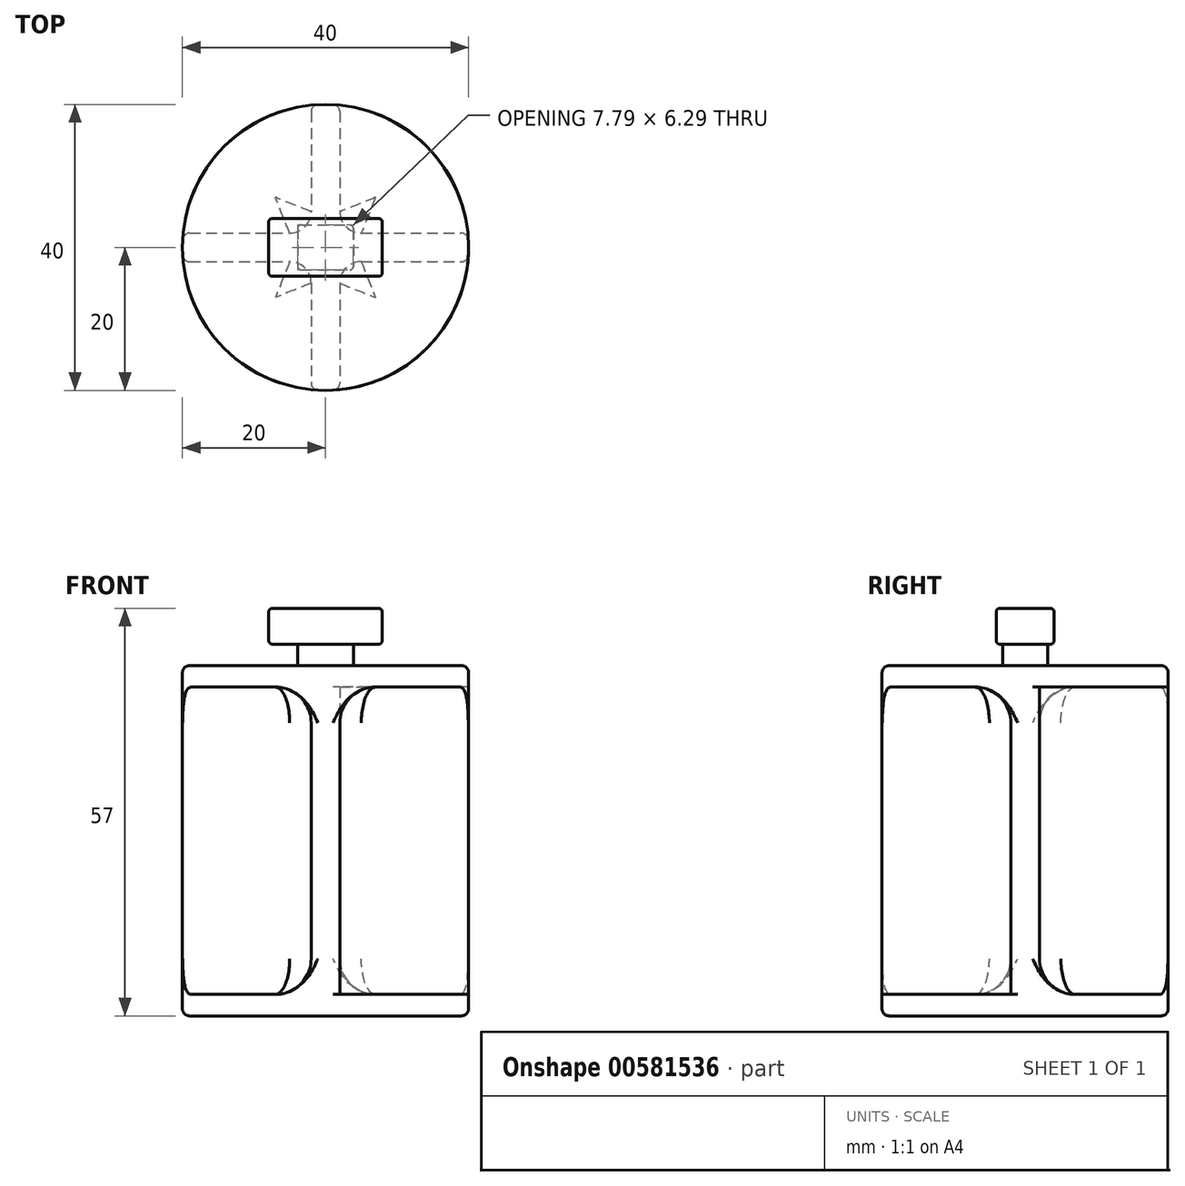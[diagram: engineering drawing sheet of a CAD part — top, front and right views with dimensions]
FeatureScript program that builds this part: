
annotation { "Feature Type Name" : "Feature", "Feature Type Description" : "" }
export const myFeature = defineFeature(function(context is Context, id is Id, definition is map)
    precondition{}
    {
        {
            var Q0;
            Q0=qCreatedBy(makeId("Top.planeOp"),FACE);
            var sketch = newSketch(context, id + "F0", { "sketchPlane" : qUnion([Q0])});
            skCircle(sketch, "E0", {"center": v(0, 0) * mm, "radius": 20 * mm});
            skLineSegment(sketch, "E1", {"start": v(0, -2) * mm, "end": v(0, -20) * mm});
            skLineSegment(sketch, "E2.0", {"start": v(-2, 20) * mm, "end": v(-2, 5) * mm});
            skLineSegment(sketch, "E3.0", {"start": v(2, 20) * mm, "end": v(2, 5) * mm});
            skLineSegment(sketch, "E4.0", {"start": v(-20, -2) * mm, "end": v(-5, -2) * mm});
            skLineSegment(sketch, "E5.0", {"start": v(-20, 2) * mm, "end": v(-5, 2) * mm});
            skPoint(sketch, "E6.orphan", {"position": v(0, 20) * mm});
            skLineSegment(sketch, "E7.trimOffspring", {"start": v(2, -5) * mm, "end": v(2, -20) * mm});
            skLineSegment(sketch, "E8.trimOffspring", {"start": v(-2, -5) * mm, "end": v(-2, -20) * mm});
            skPoint(sketch, "E9.start.orphan", {"position": v(-20, 0) * mm});
            skArc(sketch, "E10.filletArc", {"start": v(-2, -5) * mm, "mid": v(-2.88, -2.88) * mm, "end": v(-5, -2) * mm});
            skLineSegment(sketch, "E11", {"start": v(5, -2) * mm, "end": v(19.9, -2) * mm});
            skPoint(sketch, "E12.visualSharp", {"position": v(2, -2) * mm});
            skArc(sketch, "E12.filletArc", {"start": v(5, -2) * mm, "mid": v(2.88, -2.88) * mm, "end": v(2, -5) * mm});
            skArc(sketch, "E13.filletArc", {"start": v(-5, 2) * mm, "mid": v(-2.88, 2.88) * mm, "end": v(-2, 5) * mm});
            skLineSegment(sketch, "E14", {"start": v(5, 2) * mm, "end": v(19.9, 2) * mm});
            skPoint(sketch, "E15.visualSharp", {"position": v(2, 2) * mm});
            skArc(sketch, "E15.filletArc", {"start": v(2, 5) * mm, "mid": v(2.88, 2.88) * mm, "end": v(5, 2) * mm});
            skSolve(sketch);
        }
        {
            var Q0;
            {var subQ4=sQuery(id+"F0.wireOp",EDGE,"E10.filletArc");Q0=makeQuery(id+"F0.imprint","IMPRINT",FACE,{"disambiguationData":[TD([[makeQuery(id+"F0.imprint","IMPRINT",EDGE,{"derivedFrom":subQ4}),-1.0]])]});}
            extrude(context, id + "F1", {"entities" : qUnion([Q0]), "depth" : 43 * mm, "offsetDistance" : 25 * mm});
        }
        {
            var Q0;
            Q0=makeQuery(id+"F1.opExtrude","CAP_FACE",FACE,{"disambiguationData":[OSD([sQuery(id+"F0.wireOp",EDGE,"E0"),sQuery(id+"F0.wireOp",EDGE,"E2.0"),sQuery(id+"F0.wireOp",EDGE,"E3.0"),sQuery(id+"F0.wireOp",EDGE,"E4.0"),sQuery(id+"F0.wireOp",EDGE,"E5.0"),sQuery(id+"F0.wireOp",EDGE,"E7.trimOffspring"),sQuery(id+"F0.wireOp",EDGE,"E8.trimOffspring"),sQuery(id+"F0.wireOp",EDGE,"E10.filletArc"),sQuery(id+"F0.wireOp",EDGE,"E11"),sQuery(id+"F0.wireOp",EDGE,"E12.filletArc"),sQuery(id+"F0.wireOp",EDGE,"E13.filletArc"),sQuery(id+"F0.wireOp",EDGE,"E14"),sQuery(id+"F0.wireOp",EDGE,"E15.filletArc")])],"isStart":true});
            var sketch = newSketch(context, id + "F2", { "sketchPlane" : qUnion([Q0])});
            skCircle(sketch, "E16", {"center": v(0, 0) * mm, "radius": 20 * mm});
            skSolve(sketch);
        }
        {
            var Q0;
            {var subQ2=makeQuery(id+"F1.opExtrude","CAP_EDGE",EDGE,{"disambiguationData":[OSD([sQuery(id+"F0.wireOp",EDGE,"E7.trimOffspring")])],"isStart":true});Q0=makeQuery(id+"F2.imprint","IMPRINT",FACE,{"disambiguationData":[TD([[makeQuery(id+"F2.imprint","IMPRINT",EDGE,{"derivedFrom":subQ2}),-1.0]])]});}
            var Q1;
            {var subQ4=makeQuery(id+"F1.opExtrude","CAP_EDGE",EDGE,{"disambiguationData":[OSD([sQuery(id+"F0.wireOp",EDGE,"E2.0")])],"isStart":true});Q1=makeQuery(id+"F2.imprint","IMPRINT",FACE,{"disambiguationData":[TD([[makeQuery(id+"F2.imprint","IMPRINT",EDGE,{"derivedFrom":subQ4}),-1.0]])]});}
            var Q2;
            {var subQ1=makeQuery(id+"F1.opExtrude","CAP_EDGE",EDGE,{"disambiguationData":[OSD([sQuery(id+"F0.wireOp",EDGE,"E4.0")])],"isStart":true});Q2=makeQuery(id+"F2.imprint","IMPRINT",FACE,{"disambiguationData":[TD([[makeQuery(id+"F2.imprint","IMPRINT",EDGE,{"derivedFrom":subQ1}),1.0]])]});}
            var Q3;
            {var subQ1=makeQuery(id+"F1.opExtrude","CAP_EDGE",EDGE,{"disambiguationData":[OSD([sQuery(id+"F0.wireOp",EDGE,"E2.0")])],"isStart":true});Q3=makeQuery(id+"F2.imprint","IMPRINT",FACE,{"disambiguationData":[TD([[makeQuery(id+"F2.imprint","IMPRINT",EDGE,{"derivedFrom":subQ1}),1.0]])]});}
            var Q4;
            {var subQ2=makeQuery(id+"F1.opExtrude","CAP_EDGE",EDGE,{"disambiguationData":[OSD([sQuery(id+"F0.wireOp",EDGE,"E3.0")])],"isStart":true});Q4=makeQuery(id+"F2.imprint","IMPRINT",FACE,{"disambiguationData":[TD([[makeQuery(id+"F2.imprint","IMPRINT",EDGE,{"derivedFrom":subQ2}),-1.0]])]});}
            extrude(context, id + "F3", {"entities" : qUnion([Q0, Q1, Q2, Q3, Q4]), "operationType" : NewBodyOperationType.ADD, "depth" : 3 * mm, "offsetDistance" : 25 * mm});
        }
        {
            var Q0;
            Q0=makeQuery(id+"F1.opExtrude","CAP_FACE",FACE,{"disambiguationData":[OSD([sQuery(id+"F0.wireOp",EDGE,"E0"),sQuery(id+"F0.wireOp",EDGE,"E2.0"),sQuery(id+"F0.wireOp",EDGE,"E3.0"),sQuery(id+"F0.wireOp",EDGE,"E4.0"),sQuery(id+"F0.wireOp",EDGE,"E5.0"),sQuery(id+"F0.wireOp",EDGE,"E7.trimOffspring"),sQuery(id+"F0.wireOp",EDGE,"E8.trimOffspring"),sQuery(id+"F0.wireOp",EDGE,"E10.filletArc"),sQuery(id+"F0.wireOp",EDGE,"E11"),sQuery(id+"F0.wireOp",EDGE,"E12.filletArc"),sQuery(id+"F0.wireOp",EDGE,"E13.filletArc"),sQuery(id+"F0.wireOp",EDGE,"E14"),sQuery(id+"F0.wireOp",EDGE,"E15.filletArc")])],"isStart":false});
            var sketch = newSketch(context, id + "F4", { "sketchPlane" : qUnion([Q0])});
            skCircle(sketch, "E17", {"center": v(0, 0) * mm, "radius": 20 * mm});
            skSolve(sketch);
        }
        {
            var Q0;
            {var subQ1=makeQuery(id+"F1.opExtrude","CAP_EDGE",EDGE,{"disambiguationData":[OSD([sQuery(id+"F0.wireOp",EDGE,"E2.0")])],"isStart":false});Q0=makeQuery(id+"F4.imprint","IMPRINT",FACE,{"disambiguationData":[TD([[makeQuery(id+"F4.imprint","IMPRINT",EDGE,{"derivedFrom":subQ1}),-1.0]])]});}
            var Q1;
            {var subQ2=makeQuery(id+"F1.opExtrude","CAP_EDGE",EDGE,{"disambiguationData":[OSD([sQuery(id+"F0.wireOp",EDGE,"E3.0")])],"isStart":false});Q1=makeQuery(id+"F4.imprint","IMPRINT",FACE,{"disambiguationData":[TD([[makeQuery(id+"F4.imprint","IMPRINT",EDGE,{"derivedFrom":subQ2}),1.0]])]});}
            var Q2;
            {var subQ2=makeQuery(id+"F1.opExtrude","CAP_EDGE",EDGE,{"disambiguationData":[OSD([sQuery(id+"F0.wireOp",EDGE,"E7.trimOffspring")])],"isStart":false});Q2=makeQuery(id+"F4.imprint","IMPRINT",FACE,{"disambiguationData":[TD([[makeQuery(id+"F4.imprint","IMPRINT",EDGE,{"derivedFrom":subQ2}),1.0]])]});}
            var Q3;
            {var subQ1=makeQuery(id+"F1.opExtrude","CAP_EDGE",EDGE,{"disambiguationData":[OSD([sQuery(id+"F0.wireOp",EDGE,"E4.0")])],"isStart":false});Q3=makeQuery(id+"F4.imprint","IMPRINT",FACE,{"disambiguationData":[TD([[makeQuery(id+"F4.imprint","IMPRINT",EDGE,{"derivedFrom":subQ1}),-1.0]])]});}
            var Q4;
            {var subQ4=makeQuery(id+"F1.opExtrude","CAP_EDGE",EDGE,{"disambiguationData":[OSD([sQuery(id+"F0.wireOp",EDGE,"E2.0")])],"isStart":false});Q4=makeQuery(id+"F4.imprint","IMPRINT",FACE,{"disambiguationData":[TD([[makeQuery(id+"F4.imprint","IMPRINT",EDGE,{"derivedFrom":subQ4}),1.0]])]});}
            extrude(context, id + "F5", {"entities" : qUnion([Q0, Q1, Q2, Q3, Q4]), "operationType" : NewBodyOperationType.ADD, "depth" : 3 * mm, "offsetDistance" : 25 * mm});
        }
        {
            var Q0;
            Q0=makeQuery(id+"F3.opExtrude","CAP_EDGE",EDGE,{"disambiguationData":[OSD([sQuery(id+"F2.wireOp",EDGE,"E16")])],"isStart":false});
            fillet(context, id + "F6", {"entities" : qUnion([Q0]), "radius" : 1 * mm, "tangentPropagation" : true, "allowEdgeOverflow" : false});
        }
        {
            var Q0;
            Q0=makeQuery(id+"F5.opExtrude","CAP_EDGE",EDGE,{"disambiguationData":[OSD([sQuery(id+"F4.wireOp",EDGE,"E17")])],"isStart":false});
            var Q1;
            Q1=makeQuery(id+"F1.opExtrude","SWEPT_EDGE",EDGE,{"disambiguationData":[OSD([sQuery(id+"F0.wireOp",EDGE,"E0"),sQuery(id+"F0.wireOp",EDGE,"E5.0")])]});
            var Q2;
            Q2=makeQuery(id+"F1.opExtrude","SWEPT_EDGE",EDGE,{"disambiguationData":[OSD([sQuery(id+"F0.wireOp",EDGE,"E0"),sQuery(id+"F0.wireOp",EDGE,"E4.0")])]});
            var Q3;
            Q3=makeQuery(id+"F1.opExtrude","SWEPT_EDGE",EDGE,{"disambiguationData":[OSD([sQuery(id+"F0.wireOp",EDGE,"E0"),sQuery(id+"F0.wireOp",EDGE,"E2.0")])]});
            var Q4;
            Q4=makeQuery(id+"F1.opExtrude","SWEPT_EDGE",EDGE,{"disambiguationData":[OSD([sQuery(id+"F0.wireOp",EDGE,"E0"),sQuery(id+"F0.wireOp",EDGE,"E3.0")])]});
            var Q5;
            Q5=makeQuery(id+"F1.opExtrude","SWEPT_EDGE",EDGE,{"disambiguationData":[OSD([sQuery(id+"F0.wireOp",EDGE,"E0"),sQuery(id+"F0.wireOp",EDGE,"E14")])]});
            var Q6;
            Q6=makeQuery(id+"F1.opExtrude","SWEPT_EDGE",EDGE,{"disambiguationData":[OSD([sQuery(id+"F0.wireOp",EDGE,"E0"),sQuery(id+"F0.wireOp",EDGE,"E11")])]});
            var Q7;
            Q7=makeQuery(id+"F1.opExtrude","SWEPT_EDGE",EDGE,{"disambiguationData":[OSD([sQuery(id+"F0.wireOp",EDGE,"E0"),sQuery(id+"F0.wireOp",EDGE,"E7.trimOffspring")])]});
            var Q8;
            Q8=makeQuery(id+"F1.opExtrude","SWEPT_EDGE",EDGE,{"disambiguationData":[OSD([sQuery(id+"F0.wireOp",EDGE,"E0"),sQuery(id+"F0.wireOp",EDGE,"E8.trimOffspring")])]});
            fillet(context, id + "F7", {"entities" : qUnion([Q0, Q1, Q2, Q3, Q4, Q5, Q6, Q7, Q8]), "radius" : 1 * mm, "tangentPropagation" : true, "allowEdgeOverflow" : false});
        }
        {
            var Q0;
            Q0=makeQuery(id+"F5.opExtrude","CAP_FACE",FACE,{"disambiguationData":[OSD([sQuery(id+"F4.wireOp",EDGE,"E17")])],"isStart":false});
            var sketch = newSketch(context, id + "F8", { "sketchPlane" : qUnion([Q0])});
            skLineSegment(sketch, "E18.bottom", {"start": v(-3.9, 3.14) * mm, "end": v(3.9, 3.14) * mm});
            skLineSegment(sketch, "E18.top", {"start": v(-3.9, -3.14) * mm, "end": v(3.9, -3.14) * mm});
            skLineSegment(sketch, "E18.left", {"start": v(-3.9, 3.14) * mm, "end": v(-3.9, -3.14) * mm});
            skLineSegment(sketch, "E18.right", {"start": v(3.9, 3.14) * mm, "end": v(3.9, -3.14) * mm});
            skSolve(sketch);
        }
        {
            var Q0;
            Q0 = qSketchRegion(id + "F8", true);
            extrude(context, id + "F9", {"entities" : qUnion([Q0]), "operationType" : NewBodyOperationType.ADD, "depth" : 3 * mm, "offsetDistance" : 25 * mm});
        }
        {
            var Q0;
            Q0=makeQuery(id+"F9.opExtrude","CAP_FACE",FACE,{"disambiguationData":[OSD([sQuery(id+"F8.wireOp",EDGE,"E18.bottom"),sQuery(id+"F8.wireOp",EDGE,"E18.top"),sQuery(id+"F8.wireOp",EDGE,"E18.left"),sQuery(id+"F8.wireOp",EDGE,"E18.right")])],"isStart":false});
            var sketch = newSketch(context, id + "F10", { "sketchPlane" : qUnion([Q0])});
            skLineSegment(sketch, "E19.bottom", {"start": v(-7.93, 4.05) * mm, "end": v(7.93, 4.05) * mm});
            skLineSegment(sketch, "E19.top", {"start": v(-7.93, -4.05) * mm, "end": v(7.93, -4.05) * mm});
            skLineSegment(sketch, "E19.left", {"start": v(-7.93, 4.05) * mm, "end": v(-7.93, -4.05) * mm});
            skLineSegment(sketch, "E19.right", {"start": v(7.93, 4.05) * mm, "end": v(7.93, -4.05) * mm});
            skPoint(sketch, "E20", {"position": v(0, 4.05) * mm});
            skPoint(sketch, "E21", {"position": v(7.93, 0) * mm});
            skSolve(sketch);
        }
        {
            var Q0;
            Q0=makeQuery(id+"F9.opExtrude","SWEPT_EDGE",EDGE,{"disambiguationData":[OSD([sQuery(id+"F8.wireOp",EDGE,"E18.top"),sQuery(id+"F8.wireOp",EDGE,"E18.right")])]});
            fillet(context, id + "F11", {"entities" : qUnion([Q0]), "radius" : 0.5 * mm, "tangentPropagation" : true, "allowEdgeOverflow" : false});
        }
        {
            var Q0;
            Q0=makeQuery(id+"F9.opExtrude","SWEPT_EDGE",EDGE,{"disambiguationData":[OSD([sQuery(id+"F8.wireOp",EDGE,"E18.top"),sQuery(id+"F8.wireOp",EDGE,"E18.left")])]});
            var Q1;
            Q1=makeQuery(id+"F9.opExtrude","SWEPT_EDGE",EDGE,{"disambiguationData":[OSD([sQuery(id+"F8.wireOp",EDGE,"E18.bottom"),sQuery(id+"F8.wireOp",EDGE,"E18.right")])]});
            var Q2;
            Q2=makeQuery(id+"F9.opExtrude","SWEPT_EDGE",EDGE,{"disambiguationData":[OSD([sQuery(id+"F8.wireOp",EDGE,"E18.bottom"),sQuery(id+"F8.wireOp",EDGE,"E18.left")])]});
            fillet(context, id + "F12", {"entities" : qUnion([Q0, Q1, Q2]), "radius" : .5 * mm, "tangentPropagation" : true, "allowEdgeOverflow" : false});
        }
        {
            var Q0;
            Q0=makeQuery(id+"F10.imprint","IMPRINT",FACE,{"disambiguationData":[TD([[makeQuery(id+"F10.imprint","IMPRINT",EDGE,{"derivedFrom":makeQuery(id+"F9.opExtrude","CAP_EDGE",EDGE,{"disambiguationData":[OSD([sQuery(id+"F8.wireOp",EDGE,"E18.bottom")])],"isStart":false})}),-1.0]])]});
            var Q1;
            Q1=makeQuery(id+"F10.imprint","IMPRINT",FACE,{"disambiguationData":[TD([[makeQuery(id+"F10.imprint","IMPRINT",EDGE,{"derivedFrom":sQuery(id+"F10.wireOp",EDGE,"E19.bottom")}),-1.0]])]});
            extrude(context, id + "F13", {"entities" : qUnion([Q0, Q1]), "operationType" : NewBodyOperationType.ADD, "depth" : 5 * mm, "offsetDistance" : 25 * mm});
        }
        {
            var Q0;
            Q0=makeQuery(id+"F13.opExtrude","SWEPT_EDGE",EDGE,{"disambiguationData":[OSD([sQuery(id+"F10.wireOp",EDGE,"E19.top"),sQuery(id+"F10.wireOp",EDGE,"E19.left")])]});
            var Q1;
            Q1=makeQuery(id+"F13.opExtrude","CAP_EDGE",EDGE,{"disambiguationData":[OSD([sQuery(id+"F10.wireOp",EDGE,"E19.top")])],"isStart":false});
            var Q2;
            Q2=makeQuery(id+"F13.opExtrude","SWEPT_EDGE",EDGE,{"disambiguationData":[OSD([sQuery(id+"F10.wireOp",EDGE,"E19.top"),sQuery(id+"F10.wireOp",EDGE,"E19.right")])]});
            var Q3;
            Q3=makeQuery(id+"F13.opExtrude","SWEPT_EDGE",EDGE,{"disambiguationData":[OSD([sQuery(id+"F10.wireOp",EDGE,"E19.bottom"),sQuery(id+"F10.wireOp",EDGE,"E19.right")])]});
            var Q4;
            Q4=makeQuery(id+"F13.opExtrude","CAP_EDGE",EDGE,{"disambiguationData":[OSD([sQuery(id+"F10.wireOp",EDGE,"E19.right")])],"isStart":true});
            var Q5;
            Q5=makeQuery(id+"F13.opExtrude","CAP_EDGE",EDGE,{"disambiguationData":[OSD([sQuery(id+"F10.wireOp",EDGE,"E19.bottom")])],"isStart":true});
            var Q6;
            Q6=makeQuery(id+"F13.opExtrude","CAP_EDGE",EDGE,{"disambiguationData":[OSD([sQuery(id+"F10.wireOp",EDGE,"E19.top")])],"isStart":true});
            var Q7;
            Q7=makeQuery(id+"F13.opExtrude","CAP_EDGE",EDGE,{"disambiguationData":[OSD([sQuery(id+"F10.wireOp",EDGE,"E19.bottom")])],"isStart":false});
            var Q8;
            Q8=makeQuery(id+"F13.opExtrude","SWEPT_EDGE",EDGE,{"disambiguationData":[OSD([sQuery(id+"F10.wireOp",EDGE,"E19.bottom"),sQuery(id+"F10.wireOp",EDGE,"E19.left")])]});
            var Q9;
            Q9=makeQuery(id+"F13.opExtrude","CAP_EDGE",EDGE,{"disambiguationData":[OSD([sQuery(id+"F10.wireOp",EDGE,"E19.left")])],"isStart":false});
            var Q10;
            Q10=makeQuery(id+"F13.opExtrude","CAP_EDGE",EDGE,{"disambiguationData":[OSD([sQuery(id+"F10.wireOp",EDGE,"E19.left")])],"isStart":true});
            var Q11;
            Q11=makeQuery(id+"F13.opExtrude","CAP_EDGE",EDGE,{"disambiguationData":[OSD([sQuery(id+"F10.wireOp",EDGE,"E19.right")])],"isStart":false});
            fillet(context, id + "F14", {"entities" : qUnion([Q0, Q1, Q2, Q3, Q4, Q5, Q6, Q7, Q8, Q9, Q10, Q11]), "radius" : .5 * mm, "tangentPropagation" : true, "allowEdgeOverflow" : false});
        }
        {
            var Q0;
            Q0=makeQuery(id+"F1.opExtrude","CAP_EDGE",EDGE,{"disambiguationData":[OSD([sQuery(id+"F0.wireOp",EDGE,"E7.trimOffspring")])],"isStart":true});
            var Q1;
            Q1=makeQuery(id+"F1.opExtrude","CAP_EDGE",EDGE,{"disambiguationData":[OSD([sQuery(id+"F0.wireOp",EDGE,"E14")])],"isStart":true});
            var Q2;
            Q2=makeQuery(id+"F1.opExtrude","CAP_EDGE",EDGE,{"disambiguationData":[OSD([sQuery(id+"F0.wireOp",EDGE,"E2.0")])],"isStart":true});
            var Q3;
            Q3=makeQuery(id+"F1.opExtrude","CAP_EDGE",EDGE,{"disambiguationData":[OSD([sQuery(id+"F0.wireOp",EDGE,"E4.0")])],"isStart":true});
            var Q4;
            Q4=makeQuery(id+"F1.opExtrude","CAP_EDGE",EDGE,{"disambiguationData":[OSD([sQuery(id+"F0.wireOp",EDGE,"E8.trimOffspring")])],"isStart":false});
            var Q5;
            Q5=makeQuery(id+"F1.opExtrude","CAP_EDGE",EDGE,{"disambiguationData":[OSD([sQuery(id+"F0.wireOp",EDGE,"E2.0")])],"isStart":false});
            var Q6;
            Q6=makeQuery(id+"F1.opExtrude","CAP_EDGE",EDGE,{"disambiguationData":[OSD([sQuery(id+"F0.wireOp",EDGE,"E3.0")])],"isStart":false});
            var Q7;
            Q7=makeQuery(id+"F1.opExtrude","CAP_EDGE",EDGE,{"disambiguationData":[OSD([sQuery(id+"F0.wireOp",EDGE,"E7.trimOffspring")])],"isStart":false});
            fillet(context, id + "F15", {"entities" : qUnion([Q0, Q1, Q2, Q3, Q4, Q5, Q6, Q7]), "radius" : 5 * mm, "tangentPropagation" : true, "allowEdgeOverflow" : false});
        }
    });
